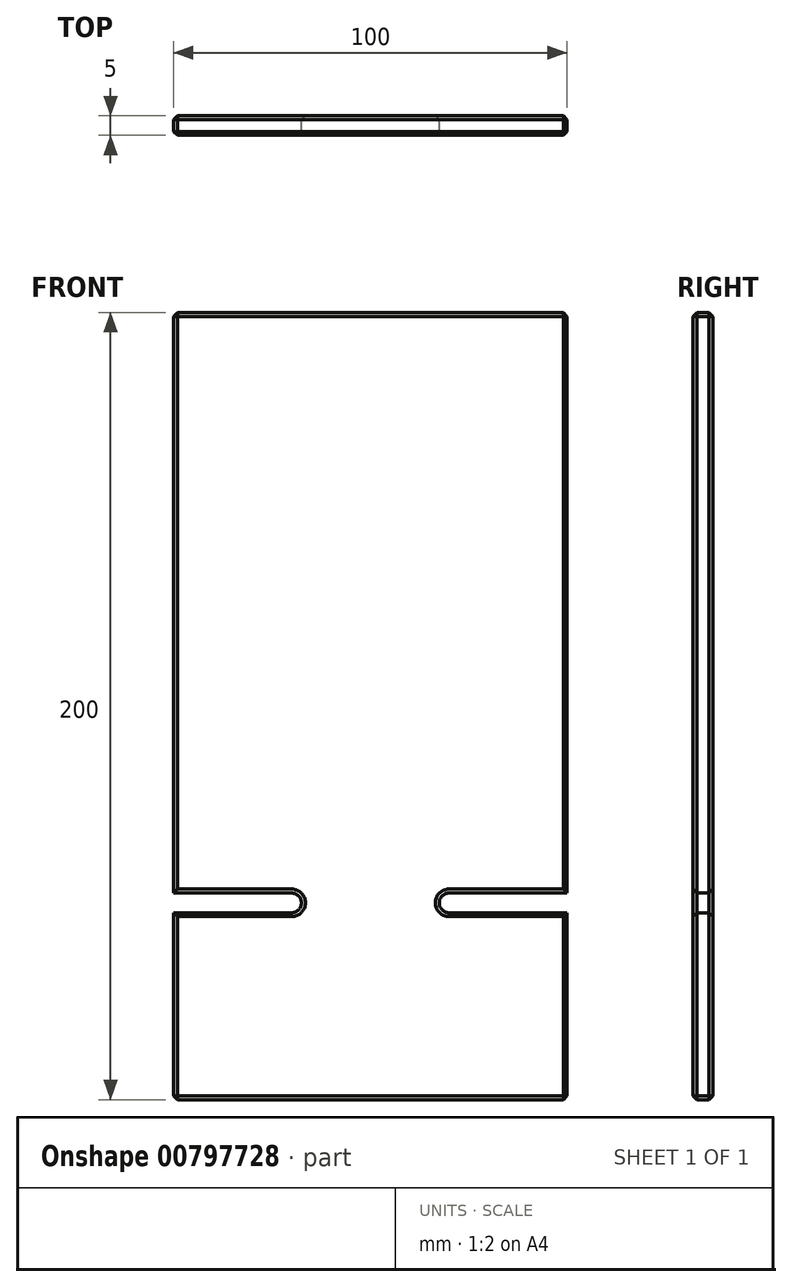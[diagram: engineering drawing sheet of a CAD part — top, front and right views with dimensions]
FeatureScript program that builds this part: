
annotation { "Feature Type Name" : "Feature", "Feature Type Description" : "" }
export const myFeature = defineFeature(function(context is Context, id is Id, definition is map)
    precondition{}
    {
        {
            var Q0;
            Q0=qCreatedBy(makeId("Front.planeOp"),FACE);
            var sketch = newSketch(context, id + "F0", { "sketchPlane" : qUnion([Q0])});
            skLineSegment(sketch, "E0.bottom", {"start": v(-20.51, 150.53) * mm, "end": v(79.49, 150.53) * mm});
            skLineSegment(sketch, "E0.top", {"start": v(-20.51, -49.47) * mm, "end": v(79.49, -49.47) * mm});
            skLineSegment(sketch, "E0.left", {"start": v(-20.51, 150.53) * mm, "end": v(-20.51, 3.03) * mm});
            skLineSegment(sketch, "E0.right", {"start": v(79.49, 150.53) * mm, "end": v(79.49, 3.03) * mm});
            skLineSegment(sketch, "E1", {"start": v(29.49, -49.47) * mm, "end": v(29.49, 0.53) * mm, "construction": true});
            skLineSegment(sketch, "E2", {"start": v(29.49, 0.53) * mm, "end": v(81.55, 0.53) * mm, "construction": true});
            skLineSegment(sketch, "E3", {"start": v(29.49, 0.53) * mm, "end": v(-40.4, 0.53) * mm, "construction": true});
            skLineSegment(sketch, "E4", {"start": v(-20.51, 0.53) * mm, "end": v(9.49, 0.53) * mm, "construction": true});
            skArc(sketch, "E5", {"start": v(9.49, -1.97) * mm, "mid": v(11.99, 0.53) * mm, "end": v(9.49, 3.03) * mm});
            skLineSegment(sketch, "E6", {"start": v(9.49, -1.97) * mm, "end": v(-20.51, -1.97) * mm});
            skLineSegment(sketch, "E7", {"start": v(9.49, 3.03) * mm, "end": v(-20.51, 3.03) * mm});
            skLineSegment(sketch, "E8.trimOffspring", {"start": v(-20.51, -1.97) * mm, "end": v(-20.51, -49.47) * mm});
            skLineSegment(sketch, "E9.MirrorCS", {"start": v(49.49, 3.03) * mm, "end": v(79.49, 3.03) * mm});
            skLineSegment(sketch, "E10.MirrorCS", {"start": v(49.49, -1.97) * mm, "end": v(79.49, -1.97) * mm});
            skArc(sketch, "E11.MirrorCS", {"start": v(49.49, -1.97) * mm, "mid": v(46.99, 0.53) * mm, "end": v(49.49, 3.03) * mm});
            skLineSegment(sketch, "E12.trimOffspring", {"start": v(79.49, -1.97) * mm, "end": v(79.49, -49.47) * mm});
            skSolve(sketch);
        }
        {
            var Q0;
            Q0 = qSketchRegion(id + "F0", true);
            extrude(context, id + "F1", {"entities" : qUnion([Q0]), "depth" : 5 * mm, "offsetDistance" : 25 * mm});
        }
        {
            var Q0;
            Q0=makeQuery(id+"F1.opExtrude","CAP_FACE",FACE,{"disambiguationData":[OSD([sQuery(id+"F0.wireOp",EDGE,"E0.bottom"),sQuery(id+"F0.wireOp",EDGE,"E0.top"),sQuery(id+"F0.wireOp",EDGE,"E0.left"),sQuery(id+"F0.wireOp",EDGE,"E0.right"),sQuery(id+"F0.wireOp",EDGE,"E5"),sQuery(id+"F0.wireOp",EDGE,"E6"),sQuery(id+"F0.wireOp",EDGE,"E7"),sQuery(id+"F0.wireOp",EDGE,"E8.trimOffspring"),sQuery(id+"F0.wireOp",EDGE,"E9.MirrorCS"),sQuery(id+"F0.wireOp",EDGE,"E10.MirrorCS"),sQuery(id+"F0.wireOp",EDGE,"E11.MirrorCS"),sQuery(id+"F0.wireOp",EDGE,"E12.trimOffspring")])],"isStart":false});
            var Q1;
            Q1=makeQuery(id+"F1.opExtrude","CAP_FACE",FACE,{"disambiguationData":[OSD([sQuery(id+"F0.wireOp",EDGE,"E0.bottom"),sQuery(id+"F0.wireOp",EDGE,"E0.top"),sQuery(id+"F0.wireOp",EDGE,"E0.left"),sQuery(id+"F0.wireOp",EDGE,"E0.right"),sQuery(id+"F0.wireOp",EDGE,"E5"),sQuery(id+"F0.wireOp",EDGE,"E6"),sQuery(id+"F0.wireOp",EDGE,"E7"),sQuery(id+"F0.wireOp",EDGE,"E8.trimOffspring"),sQuery(id+"F0.wireOp",EDGE,"E9.MirrorCS"),sQuery(id+"F0.wireOp",EDGE,"E10.MirrorCS"),sQuery(id+"F0.wireOp",EDGE,"E11.MirrorCS"),sQuery(id+"F0.wireOp",EDGE,"E12.trimOffspring")])],"isStart":true});
            var Q2;
            Q2=makeQuery(id+"F1.opExtrude","SWEPT_EDGE",EDGE,{"disambiguationData":[OSD([sQuery(id+"F0.wireOp",EDGE,"E0.top"),sQuery(id+"F0.wireOp",EDGE,"E8.trimOffspring")])]});
            var Q3;
            Q3=makeQuery(id+"F1.opExtrude","SWEPT_EDGE",EDGE,{"disambiguationData":[OSD([sQuery(id+"F0.wireOp",EDGE,"E0.top"),sQuery(id+"F0.wireOp",EDGE,"E12.trimOffspring")])]});
            var Q4;
            Q4=makeQuery(id+"F1.opExtrude","SWEPT_EDGE",EDGE,{"disambiguationData":[OSD([sQuery(id+"F0.wireOp",EDGE,"E0.bottom"),sQuery(id+"F0.wireOp",EDGE,"E0.right")])]});
            var Q5;
            Q5=makeQuery(id+"F1.opExtrude","SWEPT_EDGE",EDGE,{"disambiguationData":[OSD([sQuery(id+"F0.wireOp",EDGE,"E0.bottom"),sQuery(id+"F0.wireOp",EDGE,"E0.left")])]});
            chamfer(context, id + "F2", {"entities" : qUnion([Q0, Q1, Q2, Q3, Q4, Q5]), "width" : 1 * mm, "tangentPropagation" : true});
        }
    });
